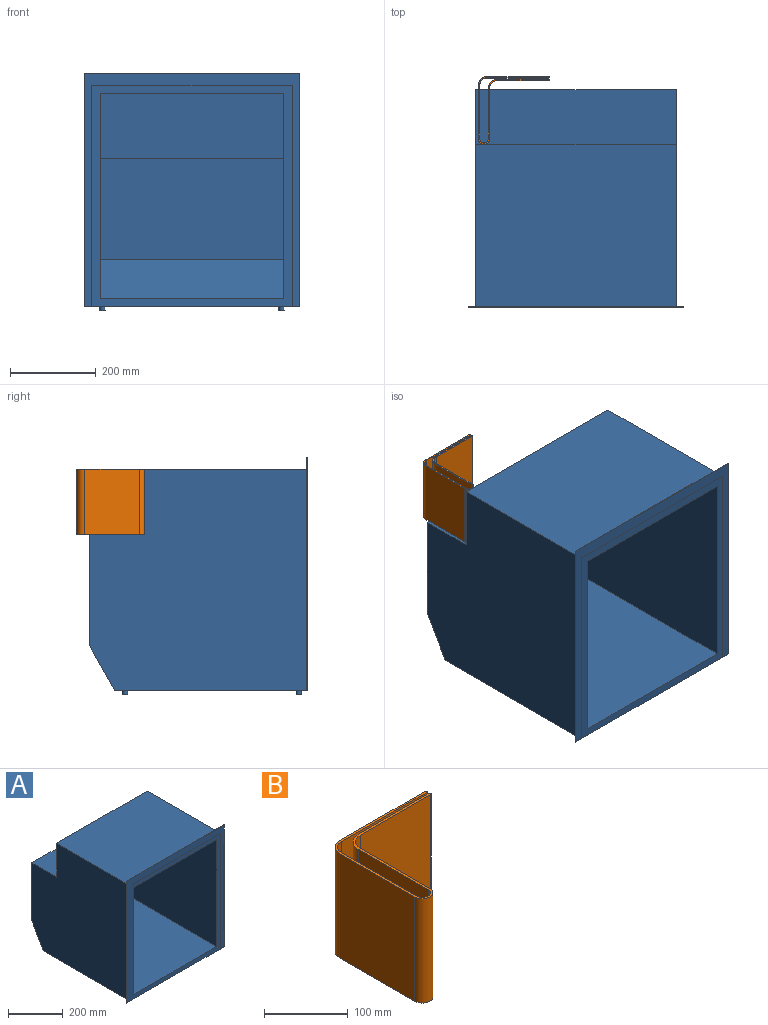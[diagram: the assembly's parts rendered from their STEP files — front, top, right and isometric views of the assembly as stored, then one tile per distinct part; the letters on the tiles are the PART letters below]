
ASSEMBLY  parts=2 mates=1
PART A: 29 faces, bbox 504.8x508.8x555.6 mm
  f0: plane 438.9x430.21mm, normal (0,0,1), area 188818.8mm2, adj f1,f6,f7,f12
  f1: plane 430.21x90.7mm, normal (0,-0.87,0.49), area 44733.9mm2, adj f0,f2,f6,f7
  f2: plane 430.21x236.32mm, normal (0,-1,0), area 101669.7mm2, adj f1,f3,f6,f7
  f3: plane 430.21x128.59mm, normal (0,0,-1), area 55319.9mm2, adj f2,f4,f6,f7
  f4: plane 430.21x152.4mm, normal (0,-1,0), area 65564.4mm2, adj f3,f5,f6,f7
  f5: plane 430.21x361.16mm, normal (0,0,-1), area 155373.9mm2, adj f4,f6,f7,f12
  f6: plane 489.74x479.43mm, normal (1,0,0), area 212892.7mm2, adj f0,f1,f2,f3,f4,f5,f12
  f7: plane 489.74x479.43mm, normal (-1,0,0), area 212892.7mm2, adj f0,f1,f2,f3,f4,f5,f12
  f8: plane 546.1x504.83mm, normal (0,1,0), area 33321.5mm2, adj f9,f10,f11,f17,f18,f19,f20
  f9: plane 504.83x0.79mm, normal (0,0,1), area 400.7mm2, adj f8,f10,f11,f12
  f10: plane 546.1x0.79mm, normal (-1,0,0), area 433.5mm2, adj f8,f9,f12,f20
  f11: plane 546.1x0.79mm, normal (1,0,0), area 433.5mm2, adj f8,f9,f12,f20
  f12: plane 546.1x504.83mm, normal (0,-1,0), area 69430.3mm2, adj f0,f5,f6,f7,f9,f10,f11,f20
  f13: plane 468.31x152.4mm, normal (0,1,0), area 71370.8mm2, adj f14,f17,f18,f19
  f14: plane 468.31x128.59mm, normal (0,0,1), area 60219.1mm2, adj f13,f15,f17,f18
  f15: plane 468.31x260.35mm, normal (0,1,0), area 121925.2mm2, adj f14,f16,f17,f18
  f16: plane 468.31x104.78mm, normal (0,0.87,-0.49), area 56251.9mm2, adj f15,f17,f18,f20
  f17: plane 517.53x508mm, normal (-1,0,0), area 240228.9mm2, adj f8,f13,f14,f15,f16,f19,f20
  f18: plane 517.53x508mm, normal (1,0,0), area 240228.9mm2, adj f8,f13,f14,f15,f16,f19,f20
  f19: plane 468.31x379.41mm, normal (0,0,1), area 177683.6mm2, adj f8,f13,f17,f18
  f20: plane 504.83x450.06mm, normal (0,0,-1), area 210289.2mm2, adj f8,f10,f11,f12,f16,f17,f18,f22
  f21: plane 12.7x12.7mm, normal (0,0,-1), area 126.7mm2, adj f22
  f22: cylinder r=6.35mm len=12.7mm, axis (0,0,-1), area 380mm2, adj f20,f21
  f23: plane 12.7x12.7mm, normal (0,0,-1), area 126.7mm2, adj f24
  f24: cylinder r=6.35mm len=12.7mm, axis (0,0,-1), area 380mm2, adj f20,f23
  f25: plane 12.7x12.7mm, normal (0,0,-1), area 126.7mm2, adj f26
  f26: cylinder r=6.35mm len=12.7mm, axis (0,0,-1), area 380mm2, adj f20,f25
  f27: plane 12.7x12.7mm, normal (0,0,-1), area 126.7mm2, adj f28
  f28: cylinder r=6.35mm len=12.7mm, axis (0,0,-1), area 380mm2, adj f20,f27
PART B: 18 faces, bbox 165.1x158.8x152.4 mm
  f0: plane 152.4x127mm, normal (1,0,0), area 19354.8mm2, adj f1,f15,f16,f17
  f1: cylinder r=15.88mm len=152.4mm, axis (0,0,-1), area 3800.3mm2, adj f0,f2,f16,f17
  f2: plane 152.4x144.46mm, normal (0,-1,0), area 22016.1mm2, adj f1,f3,f16,f17
  f3: cylinder r=1.59mm len=152.4mm, axis (0,0,-1), area 760.1mm2, adj f2,f4,f16,f17
  f4: plane 152.4x144.46mm, normal (0,1,0), area 22016.1mm2, adj f3,f5,f16,f17
  f5: cylinder r=19.05mm len=152.4mm, axis (0,0,-1), area 4560.4mm2, adj f4,f6,f16,f17
  f6: plane 152.4x127mm, normal (-1,0,0), area 19354.8mm2, adj f5,f7,f16,f17
  f7: cylinder r=12.7mm len=152.4mm, axis (0,0,-1), area 6080.5mm2, adj f6,f8,f16,f17
  f8: plane 152.4x117.48mm, normal (1,0,0), area 17903.2mm2, adj f7,f9,f16,f17
  f9: cylinder r=19.05mm len=152.4mm, axis (0,0,-1), area 4560.4mm2, adj f8,f10,f16,f17
  f10: plane 152.4x119.06mm, normal (0,-1,0), area 18145.1mm2, adj f9,f11,f16,f17
  f11: cylinder r=1.59mm len=152.4mm, axis (0,0,-1), area 760.1mm2, adj f10,f12,f16,f17
  f12: plane 152.4x119.06mm, normal (0,1,0), area 18145.1mm2, adj f11,f13,f16,f17
  f13: cylinder r=22.23mm len=152.4mm, axis (0,0,-1), area 5320.4mm2, adj f12,f14,f16,f17
  f14: plane 152.4x117.48mm, normal (-1,0,0), area 17903.2mm2, adj f13,f15,f16,f17
  f15: cylinder r=9.53mm len=152.4mm, axis (0,0,-1), area 4560.4mm2, adj f0,f14,f16,f17
  f16: plane 165.1x158.75mm, normal (0,0,1), area 1921.7mm2, adj f0,f1,f2,f3,f4,f5,f6,f7
  f17: plane 165.1x158.75mm, normal (0,0,-1), area 1921.7mm2, adj f0,f1,f2,f3,f4,f5,f6,f7
PLACE A at identity fixed
PLACE B t=(-227.81,538.17,374.65)mm
MATE fastened A.f14 <-> B.f17  axis (0,0,1) through (-234.16,443.71,374.65)mm
